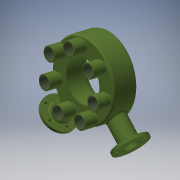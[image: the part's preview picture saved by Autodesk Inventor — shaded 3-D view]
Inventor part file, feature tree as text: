
AUTODESK INVENTOR PART (.ipt)
format: ipt  version: 2018 (Build 220112000, 112)  size: 689,152 bytes
history: native  units: mm
features: sketch x9, extrude x5, fillet x4, revolve x2, plane x2, pattern_circular x2, mirror x1, thread x1, other x1, projected_geometry x1
ambient origin geometry x8: Origin, YZ Plane, XZ Plane, XY Plane, X Axis, Y Axis, Z Axis, Center Point
bodies: Solid1 (feature_tree)
feature tree (28):
  revolve  "Revolution1"  [1 undecoded]
  plane  "Work Plane1"
  sketch  "Sketch2"  dims[d2=20.0mm d3=1.5mm]
  sketch  "Sketch3"  dims[d4=1.5mm d5=2.0mm]
  plane  "Work Plane2"
  extrude  "Extrusion1"  Depth=1.5mm
  extrude  "Extrusion2"  Depth=1.5mm
  extrude  "Extrusion3"  Depth=5.0mm
  fillet  "Fillet1"  Radius=2.0mm
  fillet  "Fillet2"  Radius=5.0mm
  fillet  "Fillet3"  Radius=7.0mm
  extrude  "Extrusion4"  [1 undecoded]
  pattern_circular  "Circular Pattern1"  Count=6  [1 undecoded]
  mirror  "Mirror1"
  revolve  "Revolution2"  Angle=45.0deg
  extrude  "Extrusion5"  Depth=18.0mm
  fillet  "Fillet4"  Radius=10.0mm
  thread  "Thread1"  [1 undecoded]
  other  "Work Axis1"
  pattern_circular  "Circular Pattern2"  [2 undecoded]
  sketch  "Sketch1"  dims[d0=24.0mm d1=37.5mm]
  sketch  "Sketch4"  dims[d6=2.0mm d7=1.0mm d8=2.0mm d9=5.0mm d10=7.0mm]
  sketch  "Sketch5"  dims[d11=90.0deg d12=-12.0mm d13=60.0mm]
  sketch  "Sketch6"  dims[d14=45.0deg d15=45.0deg]
  sketch  "Sketch7"  dims[d16=15.0mm d17=18.0mm d18=10.0mm d19=0.0mm d20=34.0mm]
  sketch  "Sketch8"  dims[d21=3.0mm d22=0.0mm]
  sketch  "Sketch9"  dims[d23=32.75mm d24=0.0mm d25=4.0mm d26=1.5mm d27=2.0mm d28=13.0mm d29=3.0mm d30=6.75mm d31=0.0mm d32=50.0mm d33=360.0deg d36=2.0mm d37=30.2mm d38=3.5mm d39=4.5mm d40=6.0mm d41=7.0mm d43=12.5mm d44=11.5mm d45=0.25mm d46=0.25mm d47=1.25mm d48=1.0mm d49=90.0deg d50=10.25mm d51=0.0mm d52=1.5mm d53=10.0mm d54=0.0mm d55=70.0mm d56=360.0deg]
  projected_geometry  "Projected Loop1"
note: 6 required parameter values undecoded (feature->parameter linkage not recoverable at this tier; creation-order binding heuristic only, values carry confidence <= 0.55)